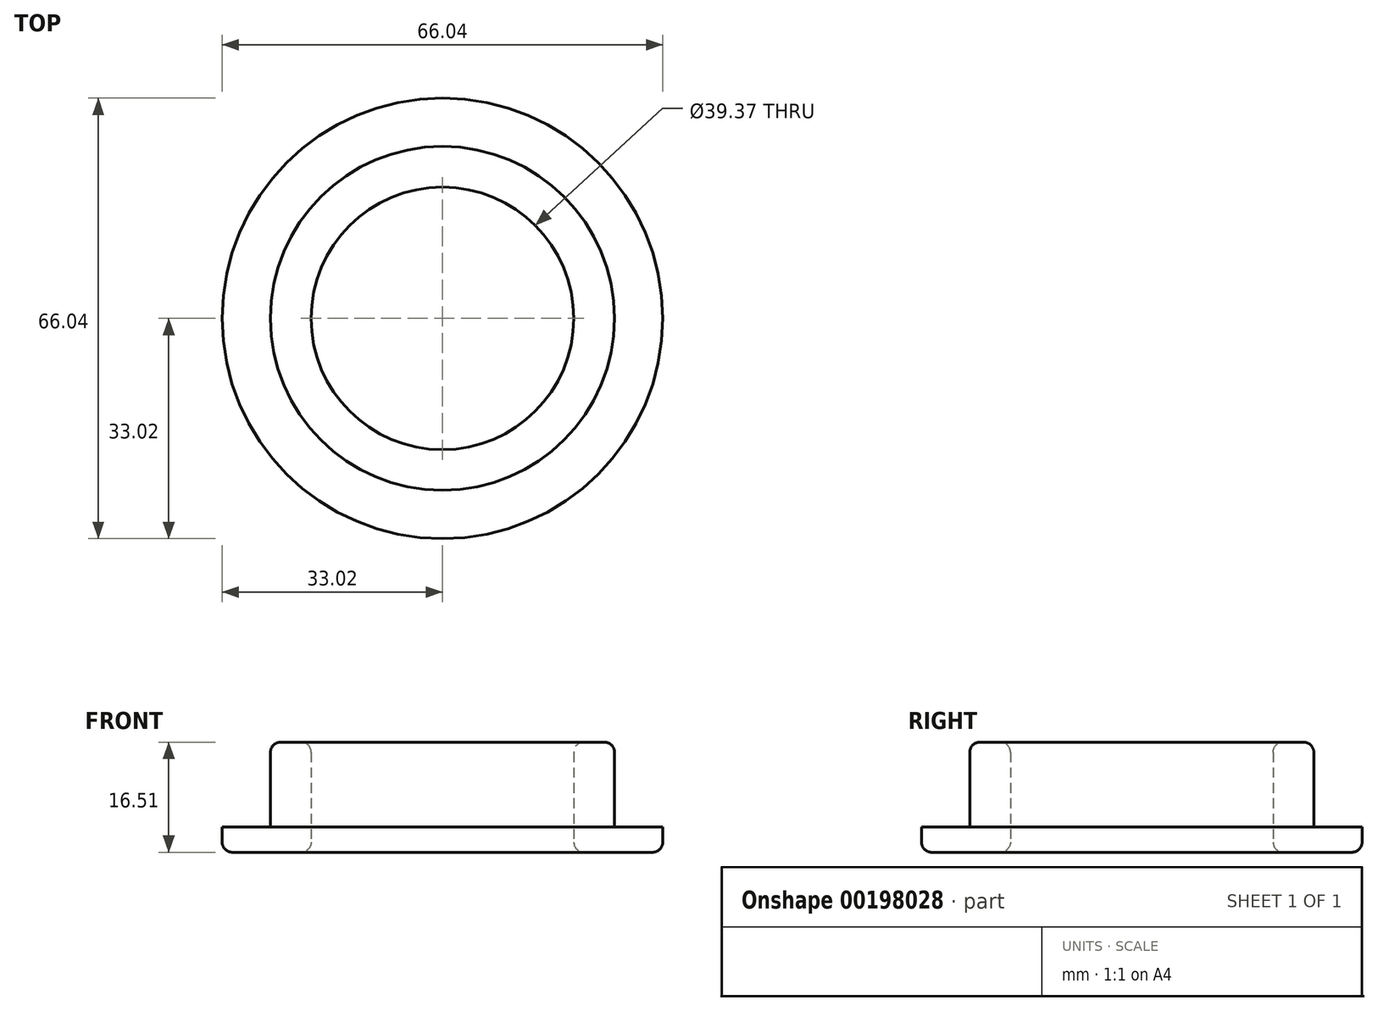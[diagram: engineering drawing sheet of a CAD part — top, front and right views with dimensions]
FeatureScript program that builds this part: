
annotation { "Feature Type Name" : "Feature", "Feature Type Description" : "" }
export const myFeature = defineFeature(function(context is Context, id is Id, definition is map)
    precondition{}
    {
        {
            var Q0;
            Q0=qCreatedBy(makeId("Top.planeOp"),FACE);
            var sketch = newSketch(context, id + "F0", { "sketchPlane" : qUnion([Q0])});
            skCircle(sketch, "E0", {"center": v(0, 0) * mm, "radius": 33.02 * mm});
            skCircle(sketch, "E1", {"center": v(0, 0) * mm, "radius": 19.69 * mm});
            skSolve(sketch);
        }
        {
            var Q0;
            Q0 = qSketchRegion(id + "F0", true);
            extrude(context, id + "F1", {"entities" : qUnion([Q0]), "depth" : 3.8 * mm});
        }
        {
            var Q0;
            Q0=makeQuery(id+"F1.opExtrude","CAP_FACE",FACE,{"disambiguationData":[OSD([sQuery(id+"F0.wireOp",EDGE,"E0"),sQuery(id+"F0.wireOp",EDGE,"E1")])],"isStart":false});
            var sketch = newSketch(context, id + "F2", { "sketchPlane" : qUnion([Q0])});
            skCircle(sketch, "E2", {"center": v(0, 0) * mm, "radius": 19.69 * mm});
            skCircle(sketch, "E3", {"center": v(0, 0) * mm, "radius": 25.78 * mm});
            skSolve(sketch);
        }
        {
            var Q0;
            Q0 = qSketchRegion(id + "F2", true);
            extrude(context, id + "F3", {"entities" : qUnion([Q0]), "operationType" : NewBodyOperationType.ADD, "depth" : 12.7 * mm});
        }
        {
            var Q0;
            Q0=makeQuery(id+"F1.opExtrude","CAP_EDGE",EDGE,{"disambiguationData":[OSD([sQuery(id+"F0.wireOp",EDGE,"E0")])],"isStart":true});
            var Q1;
            Q1=makeQuery(id+"F1.opExtrude","CAP_EDGE",EDGE,{"disambiguationData":[OSD([sQuery(id+"F0.wireOp",EDGE,"E1")])],"isStart":true});
            var Q2;
            Q2=makeQuery(id+"F3.opExtrude","CAP_EDGE",EDGE,{"disambiguationData":[OSD([sQuery(id+"F2.wireOp",EDGE,"E3")])],"isStart":false});
            var Q3;
            Q3=makeQuery(id+"F3.opExtrude","CAP_EDGE",EDGE,{"disambiguationData":[OSD([sQuery(id+"F2.wireOp",EDGE,"E2")])],"isStart":false});
            fillet(context, id + "F4", {"entities" : qUnion([Q0, Q1, Q2, Q3]), "radius" : 1.52 * mm, "tangentPropagation" : true, "allowEdgeOverflow" : false});
        }
    });
